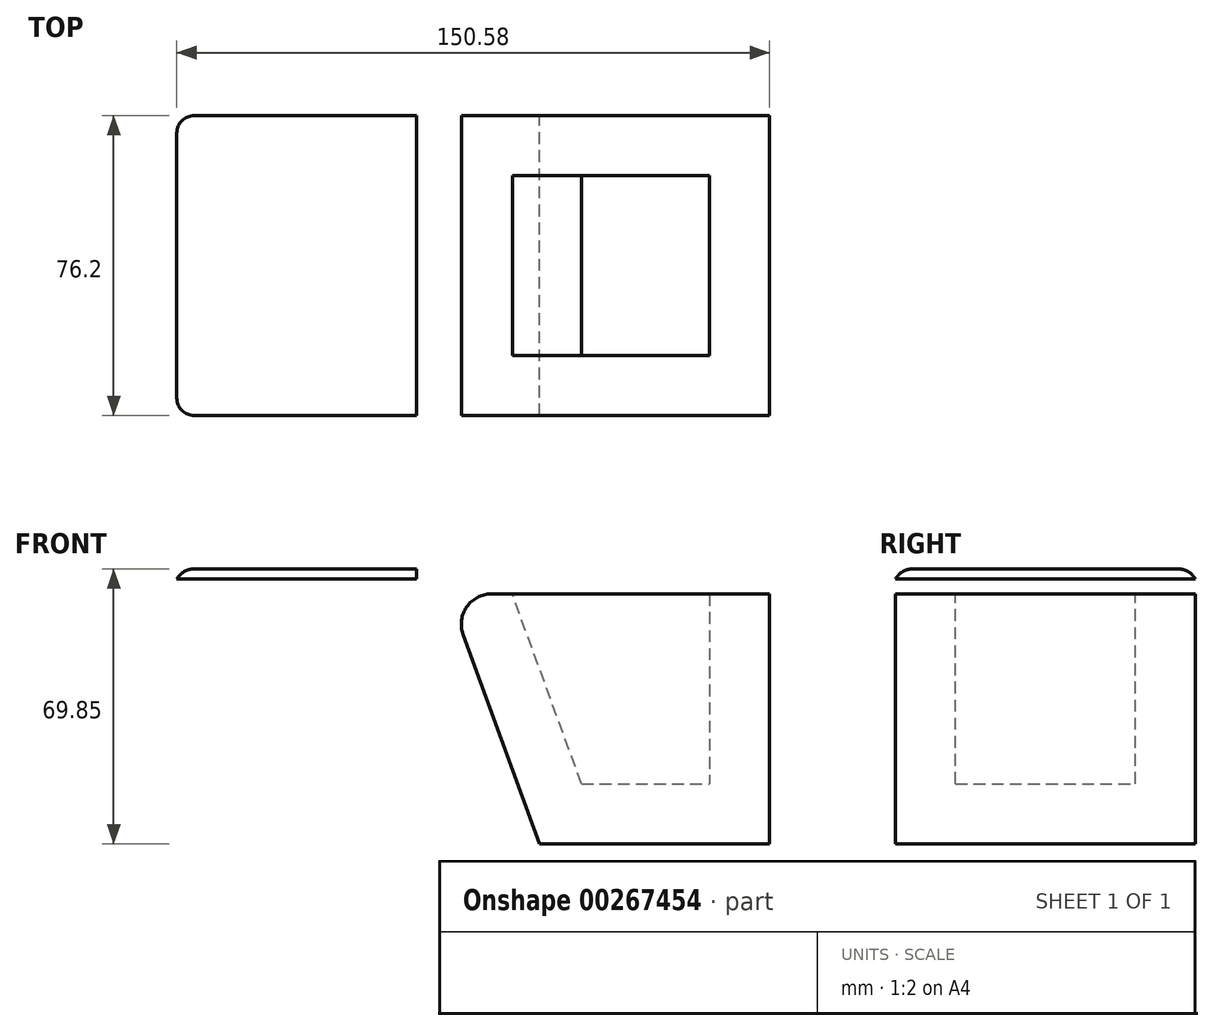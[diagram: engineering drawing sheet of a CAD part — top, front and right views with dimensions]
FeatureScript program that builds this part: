
annotation { "Feature Type Name" : "Feature", "Feature Type Description" : "" }
export const myFeature = defineFeature(function(context is Context, id is Id, definition is map)
    precondition{}
    {
        {
            var Q0;
            Q0=qCreatedBy(makeId("Front.planeOp"),FACE);
            var sketch = newSketch(context, id + "F0", { "sketchPlane" : qUnion([Q0])});
            skLineSegment(sketch, "E0.bottom", {"start": v(0, 0) * mm, "end": v(58.42, 0) * mm});
            skLineSegment(sketch, "E0.top", {"start": v(0, -63.5) * mm, "end": v(58.42, -63.5) * mm});
            skLineSegment(sketch, "E0.left", {"start": v(0, 0) * mm, "end": v(0, -63.5) * mm});
            skLineSegment(sketch, "E0.right", {"start": v(58.42, 0) * mm, "end": v(58.42, -63.5) * mm});
            skLineSegment(sketch, "E1", {"start": v(0, -63.5) * mm, "end": v(-19.41, -10.23) * mm});
            skLineSegment(sketch, "E2", {"start": v(-12.25, 0) * mm, "end": v(0, 0) * mm});
            skLineSegment(sketch, "E3.bottom", {"start": v(58.42, 0) * mm, "end": v(33.02, 0) * mm});
            skLineSegment(sketch, "E3.top", {"start": v(58.42, 58.42) * mm, "end": v(40.64, 58.42) * mm});
            skLineSegment(sketch, "E3.left", {"start": v(58.42, 0) * mm, "end": v(58.42, 58.42) * mm});
            skLineSegment(sketch, "E3.right", {"start": v(33.02, 0) * mm, "end": v(33.02, 50.8) * mm});
            skPoint(sketch, "E4.visualSharp", {"position": v(-23.14, 0) * mm});
            skArc(sketch, "E4.filletArc", {"start": v(-12.25, 0) * mm, "mid": v(-18.5, -3.25) * mm, "end": v(-19.41, -10.23) * mm});
            skPoint(sketch, "E5.visualSharp", {"position": v(33.02, 58.42) * mm});
            skArc(sketch, "E5.filletArc", {"start": v(40.64, 58.42) * mm, "mid": v(35.25, 56.19) * mm, "end": v(33.02, 50.8) * mm});
            skArc(sketch, "E6", {"start": v(27.87, -27.75) * mm, "mid": v(34.18, -14.57) * mm, "end": v(33.02, 0) * mm});
            skArc(sketch, "E7", {"start": v(5.23, -27.75) * mm, "mid": v(10.93, -35.14) * mm, "end": v(20.23, -34.41) * mm});
            skLineSegment(sketch, "E8", {"start": v(0, 0) * mm, "end": v(5.23, -27.75) * mm});
            skLineSegment(sketch, "E9", {"start": v(20.23, -34.41) * mm, "end": v(36.99, -44.78) * mm});
            skLineSegment(sketch, "E10", {"start": v(36.99, -44.78) * mm, "end": v(43.4, -34.41) * mm});
            skLineSegment(sketch, "E11", {"start": v(43.4, -34.41) * mm, "end": v(49.54, -34.41) * mm});
            skLineSegment(sketch, "E12", {"start": v(49.54, -34.41) * mm, "end": v(49.54, -63.5) * mm});
            skLineSegment(sketch, "E13", {"start": v(55.33, -63.5) * mm, "end": v(55.33, -26.77) * mm});
            skLineSegment(sketch, "E14", {"start": v(55.33, -26.77) * mm, "end": v(43.67, -26.77) * mm});
            skLineSegment(sketch, "E15", {"start": v(43.67, -26.77) * mm, "end": v(35.88, -36.45) * mm});
            skLineSegment(sketch, "E16", {"start": v(35.88, -36.45) * mm, "end": v(27.87, -27.75) * mm});
            skLineSegment(sketch, "E17", {"start": v(27.87, -27.75) * mm, "end": v(20.23, -34.41) * mm});
            skSolve(sketch);
        }
        {
            var Q0;
            Q0=makeQuery(id+"F0.imprint","IMPRINT",FACE,{"disambiguationData":[TD([[makeQuery(id+"F0.imprint","IMPRINT",EDGE,{"derivedFrom":sQuery(id+"F0.wireOp",EDGE,"E3.bottom")}),-1.0]])]});
            var Q1;
            Q1=makeQuery(id+"F0.imprint","IMPRINT",FACE,{"disambiguationData":[TD([[makeQuery(id+"F0.imprint","IMPRINT",EDGE,{"derivedFrom":sQuery(id+"F0.wireOp",EDGE,"E0.left")}),-1.0]])]});
            var Q2;
            {var subQ0=sQuery(id+"F0.wireOp",EDGE,"E0.left");Q2=makeQuery(id+"F0.imprint","IMPRINT",FACE,{"disambiguationData":[TD([[makeQuery(id+"F0.imprint","IMPRINT",EDGE,{"derivedFrom":subQ0}),1.0]])]});}
            var Q3;
            {var subQ1=sQuery(id+"F0.wireOp",EDGE,"E0.right");Q3=makeQuery(id+"F0.imprint","IMPRINT",FACE,{"disambiguationData":[TD([[makeQuery(id+"F0.imprint","IMPRINT",EDGE,{"derivedFrom":subQ1}),-1.0]])]});}
            var Q4;
            Q4=makeQuery(id+"F0.imprint","IMPRINT",FACE,{"disambiguationData":[TD([[makeQuery(id+"F0.imprint","IMPRINT",EDGE,{"derivedFrom":sQuery(id+"F0.wireOp",EDGE,"E0.bottom")}),-1.0]])]});
            var Q5;
            Q5=makeQuery(id+"F0.imprint","IMPRINT",FACE,{"disambiguationData":[TD([[makeQuery(id+"F0.imprint","IMPRINT",EDGE,{"derivedFrom":sQuery(id+"F0.wireOp",EDGE,"E9")}),1.0]])]});
            extrude(context, id + "F1", {"entities" : qUnion([Q0, Q1, Q2, Q3, Q4, Q5]), "endBound" : BoundingType.SYMMETRIC, "depth" : 76.2 * mm});
        }
        {
            var Q0;
            Q0=makeQuery(id+"F1.opExtrude","SWEPT_FACE",FACE,{"disambiguationData":[OSD([sQuery(id+"F0.wireOp",EDGE,"E0.bottom"),sQuery(id+"F0.wireOp",EDGE,"E2")])]});
            shell(context, id + "F2", {"entities" : qUnion([Q0]), "thickness" : 15.24 * mm});
        }
        {
            var Q0;
            Q0=qCreatedBy(makeId("Front.planeOp"),FACE);
            var sketch = newSketch(context, id + "F3", { "sketchPlane" : qUnion([Q0])});
            skLineSegment(sketch, "E18.bottom", {"start": v(-31.2, 3.8) * mm, "end": v(-92.16, 3.8) * mm});
            skLineSegment(sketch, "E18.top", {"start": v(-31.2, 6.35) * mm, "end": v(-92.16, 6.35) * mm});
            skLineSegment(sketch, "E18.left", {"start": v(-31.2, 3.8) * mm, "end": v(-31.2, 6.35) * mm});
            skLineSegment(sketch, "E18.right", {"start": v(-92.16, 3.8) * mm, "end": v(-92.16, 6.35) * mm});
            skSolve(sketch);
        }
        {
            var Q0;
            Q0=makeQuery(id+"F3.imprint","IMPRINT",FACE,{"disambiguationData":[TD([[makeQuery(id+"F3.imprint","IMPRINT",EDGE,{"derivedFrom":sQuery(id+"F3.wireOp",EDGE,"E18.bottom")}),-1.0]])]});
            extrude(context, id + "F4", {"entities" : qUnion([Q0]), "endBound" : BoundingType.SYMMETRIC, "depth" : 76.2 * mm});
        }
        {
            var Q0;
            Q0=makeQuery(id+"F4.opExtrude","SWEPT_EDGE",EDGE,{"disambiguationData":[OSD([sQuery(id+"F3.wireOp",EDGE,"E18.top"),sQuery(id+"F3.wireOp",EDGE,"E18.right")])]});
            var Q1;
            Q1=makeQuery(id+"F4.opExtrude","CAP_EDGE",EDGE,{"disambiguationData":[OSD([sQuery(id+"F3.wireOp",EDGE,"E18.top")])],"isStart":false});
            var Q2;
            Q2=makeQuery(id+"F4.opExtrude","CAP_EDGE",EDGE,{"disambiguationData":[OSD([sQuery(id+"F3.wireOp",EDGE,"E18.top")])],"isStart":true});
            fillet(context, id + "F5", {"entities" : qUnion([Q0, Q1, Q2]), "radius" : 5.08 * mm, "tangentPropagation" : true, "allowEdgeOverflow" : false});
        }
        {
            var Q0;
            {var subQ0=sQuery(id+"F3.wireOp",EDGE,"E18.top");Q0=makeQuery(id+"F5.opFillet","BLEND_EDGE",EDGE,{"blendedFrom":[makeQuery(id+"F4.opExtrude","SWEPT_EDGE",EDGE,{"disambiguationData":[OSD([subQ0,sQuery(id+"F3.wireOp",EDGE,"E18.right")])]}),makeQuery(id+"F4.opExtrude","CAP_EDGE",EDGE,{"disambiguationData":[OSD([subQ0])],"isStart":false})],"blendedInto":[]});}
            var Q1;
            {var subQ0=sQuery(id+"F3.wireOp",EDGE,"E18.top");Q1=makeQuery(id+"F5.opFillet","BLEND_EDGE",EDGE,{"blendedFrom":[makeQuery(id+"F4.opExtrude","SWEPT_EDGE",EDGE,{"disambiguationData":[OSD([subQ0,sQuery(id+"F3.wireOp",EDGE,"E18.right")])]}),makeQuery(id+"F4.opExtrude","CAP_EDGE",EDGE,{"disambiguationData":[OSD([subQ0])],"isStart":true})],"blendedInto":[]});}
            fillet(context, id + "F6", {"entities" : qUnion([Q0, Q1]), "radius" : 5.08 * mm, "tangentPropagation" : true, "allowEdgeOverflow" : false});
        }
    });
